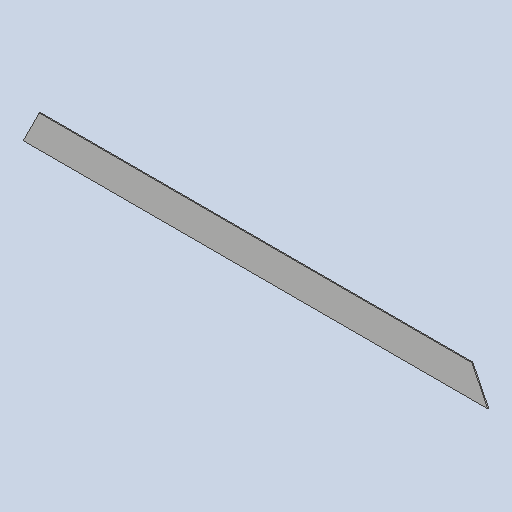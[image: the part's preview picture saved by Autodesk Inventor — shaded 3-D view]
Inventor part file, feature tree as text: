
AUTODESK INVENTOR PART (.ipt)
format: ipt  version: 2025 (Build 290162010, 162A)  size: 276,480 bytes
history: native  units: mm
features: other x2, sheet_metal_op x1, sketch x1
ambient origin geometry x8: Origin, YZ Plane, XZ Plane, XY Plane, X Axis, Y Axis, Z Axis, Center Point
bodies: Solid1 (feature_tree)
feature tree (4):
  sheet_metal_op  "Face1"
  sketch  "Sketch1"  dims[d0=100.0mm d1=1800.0mm d2=3.0mm d3=20.333086mm d6=675.5mm d7=20.333086mm d8=675.5mm]
  other  "Plate1"
  other  "Definition1"
